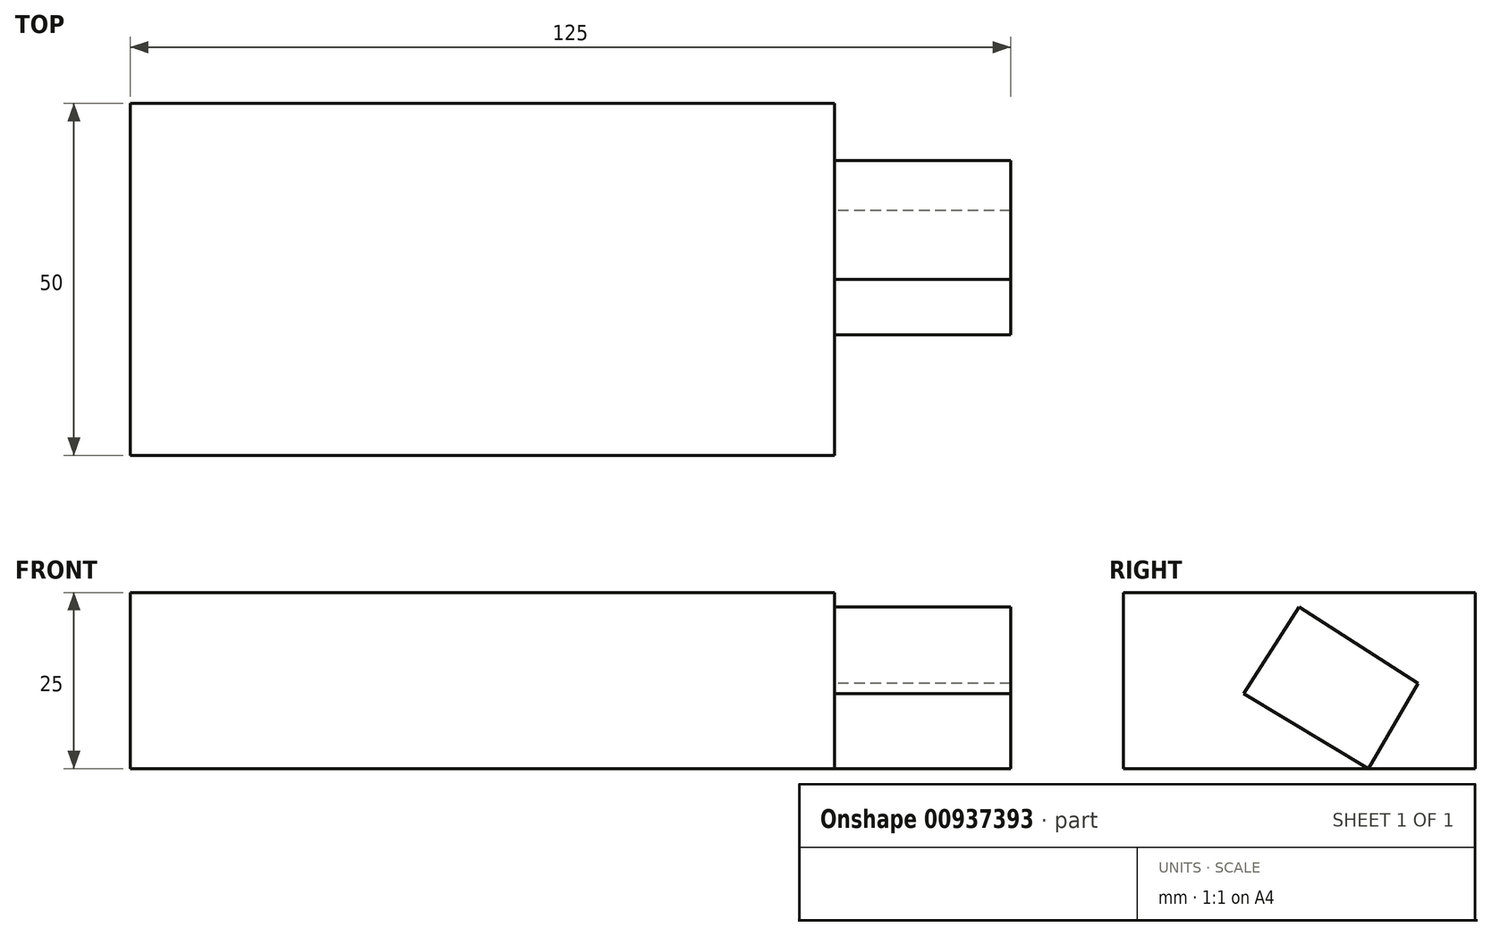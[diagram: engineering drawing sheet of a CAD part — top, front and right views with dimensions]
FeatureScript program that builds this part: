
annotation { "Feature Type Name" : "Feature", "Feature Type Description" : "" }
export const myFeature = defineFeature(function(context is Context, id is Id, definition is map)
    precondition{}
    {
        {
            var Q0;
            Q0=qCreatedBy(makeId("Top.planeOp"),FACE);
            var sketch = newSketch(context, id + "F0", { "sketchPlane" : qUnion([Q0])});
            skLineSegment(sketch, "E0.bottom", {"start": v(0, 0) * mm, "end": v(100, 0) * mm});
            skLineSegment(sketch, "E0.top", {"start": v(0, 50) * mm, "end": v(100, 50) * mm});
            skLineSegment(sketch, "E0.left", {"start": v(0, 0) * mm, "end": v(0, 50) * mm});
            skLineSegment(sketch, "E0.right", {"start": v(100, 0) * mm, "end": v(100, 50) * mm});
            skSolve(sketch);
        }
        {
            var Q0;
            Q0=makeQuery(id+"F0.imprint","IMPRINT",FACE,{"disambiguationData":[TD([[makeQuery(id+"F0.imprint","IMPRINT",EDGE,{"derivedFrom":sQuery(id+"F0.wireOp",EDGE,"E0.bottom")}),1.0]])]});
            extrude(context, id + "F1", {"entities" : qUnion([Q0]), "depth" : 25 * mm, "offsetDistance" : 25 * mm});
        }
        {
            var Q0;
            Q0=makeQuery(id+"F1.opExtrude","SWEPT_FACE",FACE,{"disambiguationData":[OSD([sQuery(id+"F0.wireOp",EDGE,"E0.right")])]});
            var sketch = newSketch(context, id + "F2", { "sketchPlane" : qUnion([Q0])});
            skLineSegment(sketch, "E1", {"start": v(17.11, 10.66) * mm, "end": v(25, 22.94) * mm});
            skPoint(sketch, "E1.endSnap0", {"position": v(25, 0) * mm});
            skLineSegment(sketch, "E2", {"start": v(25, 22.94) * mm, "end": v(41.88, 12.1) * mm});
            skLineSegment(sketch, "E3", {"start": v(41.88, 12.1) * mm, "end": v(34.79, 0) * mm});
            skLineSegment(sketch, "E4", {"start": v(34.79, 0) * mm, "end": v(17.11, 10.66) * mm});
            skSolve(sketch);
        }
        {
            var Q0;
            Q0=makeQuery(id+"F2.imprint","IMPRINT",FACE,{"disambiguationData":[TD([[makeQuery(id+"F2.imprint","IMPRINT",EDGE,{"derivedFrom":sQuery(id+"F2.wireOp",EDGE,"E1")}),-1.0]])]});
            extrude(context, id + "F3", {"entities" : qUnion([Q0]), "operationType" : NewBodyOperationType.ADD, "oppositeDirection" : true, "depth" : -25 * mm, "offsetDistance" : 25 * mm});
        }
    });
